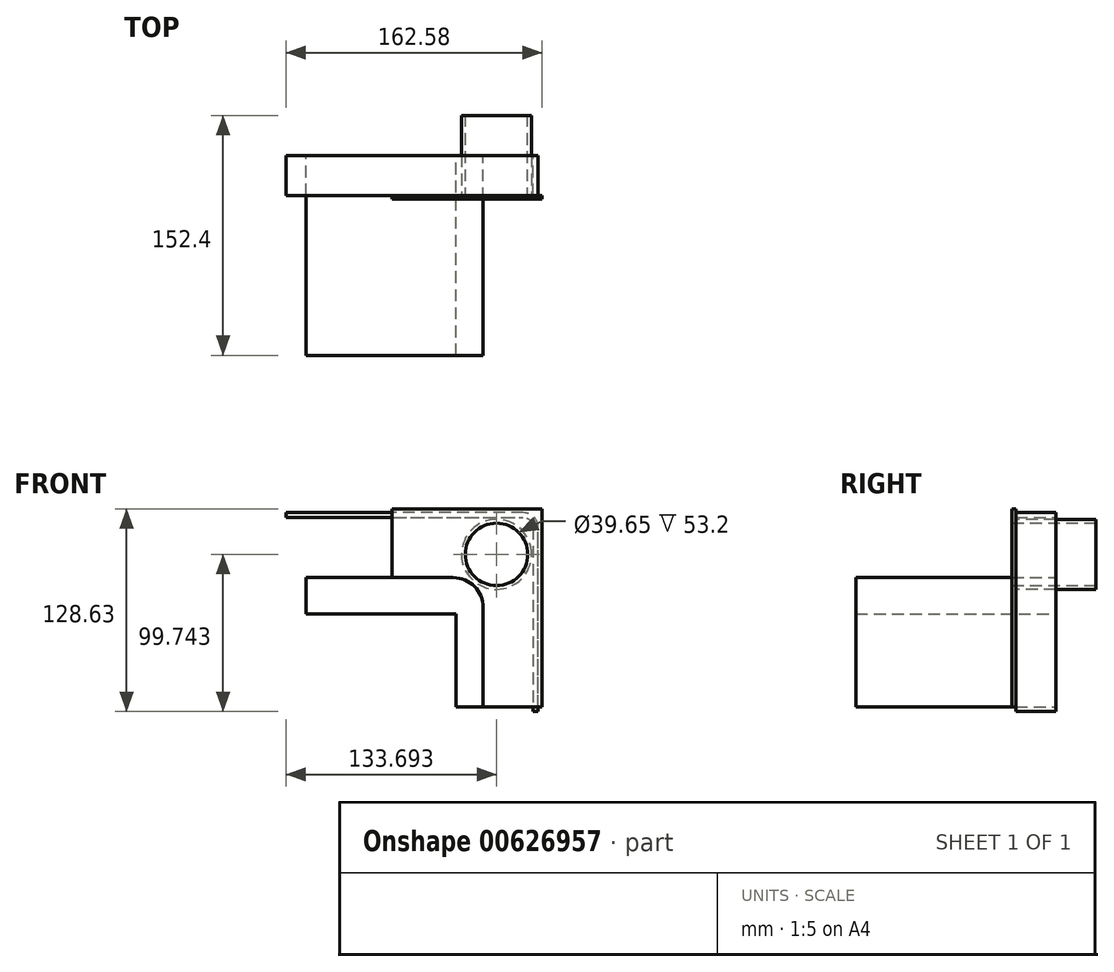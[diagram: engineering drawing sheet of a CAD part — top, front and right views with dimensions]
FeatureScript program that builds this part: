
annotation { "Feature Type Name" : "Feature", "Feature Type Description" : "" }
export const myFeature = defineFeature(function(context is Context, id is Id, definition is map)
    precondition{}
    {
        {
            var Q0;
            Q0=qCreatedBy(makeId("Front.planeOp"),FACE);
            var sketch = newSketch(context, id + "F0", { "sketchPlane" : qUnion([Q0])});
            skLineSegment(sketch, "E0", {"start": v(-125.26, 38.1) * mm, "end": v(25.4, 38.1) * mm});
            skLineSegment(sketch, "E1", {"start": v(31.75, 31.75) * mm, "end": v(31.75, -84.96) * mm});
            skLineSegment(sketch, "E2", {"start": v(31.75, -84.96) * mm, "end": v(34.92, -84.96) * mm});
            skLineSegment(sketch, "E3", {"start": v(34.92, -84.96) * mm, "end": v(34.92, 31.75) * mm});
            skLineSegment(sketch, "E4", {"start": v(25.4, 41.28) * mm, "end": v(-125.26, 41.27) * mm});
            skLineSegment(sketch, "E5", {"start": v(-125.26, 41.27) * mm, "end": v(-125.26, 38.1) * mm});
            skLineSegment(sketch, "E6", {"start": v(0, -19.05) * mm, "end": v(0, -82.22) * mm});
            skLineSegment(sketch, "E7", {"start": v(-19.05, 0) * mm, "end": v(-112.52, 0) * mm});
            skLineSegment(sketch, "E8", {"start": v(-112.52, 0) * mm, "end": v(-112.52, -22.95) * mm});
            skLineSegment(sketch, "E9", {"start": v(-112.52, -22.95) * mm, "end": v(-17.27, -22.95) * mm});
            skLineSegment(sketch, "E10", {"start": v(-17.27, -22.95) * mm, "end": v(-17.27, -82.22) * mm});
            skLineSegment(sketch, "E11", {"start": v(-17.27, -82.22) * mm, "end": v(0, -82.22) * mm});
            skPoint(sketch, "E12.visualSharp", {"position": v(31.75, 38.1) * mm});
            skArc(sketch, "E12.filletArc", {"start": v(31.75, 31.75) * mm, "mid": v(29.9, 36.24) * mm, "end": v(25.4, 38.1) * mm});
            skArc(sketch, "E13", {"start": v(25.4, 41.28) * mm, "mid": v(32.14, 38.49) * mm, "end": v(34.93, 31.75) * mm});
            skPoint(sketch, "E14.visualSharp", {"position": v(0, 0) * mm});
            skArc(sketch, "E14.filletArc", {"start": v(0, -19.05) * mm, "mid": v(-5.58, -5.58) * mm, "end": v(-19.05, 0) * mm});
            skSolve(sketch);
        }
        {
            var Q0;
            Q0=makeQuery(id+"F0.imprint","IMPRINT",FACE,{"disambiguationData":[TD([[makeQuery(id+"F0.imprint","IMPRINT",EDGE,{"derivedFrom":sQuery(id+"F0.wireOp",EDGE,"E6")}),-1.0]])]});
            extrude(context, id + "F1", {"entities" : qUnion([Q0]), "depth" : 127 * mm, "offsetDistance" : 25 * mm});
        }
        {
            var Q0;
            Q0=makeQuery(id+"F0.imprint","IMPRINT",FACE,{"disambiguationData":[TD([[makeQuery(id+"F0.imprint","IMPRINT",EDGE,{"derivedFrom":sQuery(id+"F0.wireOp",EDGE,"E0")}),1.0]])]});
            extrude(context, id + "F2", {"entities" : qUnion([Q0]), "depth" : 25.4 * mm, "offsetDistance" : 25 * mm});
        }
        {
            var Q0;
            Q0=makeQuery(id+"F2.opExtrude","CAP_FACE",FACE,{"disambiguationData":[OSD([sQuery(id+"F0.wireOp",EDGE,"E0"),sQuery(id+"F0.wireOp",EDGE,"E1"),sQuery(id+"F0.wireOp",EDGE,"E2"),sQuery(id+"F0.wireOp",EDGE,"E3"),sQuery(id+"F0.wireOp",EDGE,"E4"),sQuery(id+"F0.wireOp",EDGE,"E5"),sQuery(id+"F0.wireOp",EDGE,"E12.filletArc"),sQuery(id+"F0.wireOp",EDGE,"E13")])],"isStart":false});
            var sketch = newSketch(context, id + "F3", { "sketchPlane" : qUnion([Q0])});
            skCircle(sketch, "E15", {"center": v(8.43, 14.78) * mm, "radius": 22.23 * mm});
            skLineSegment(sketch, "E16", {"start": v(0, 0) * mm, "end": v(34.92, 41.28) * mm, "construction": true});
            skLineSegment(sketch, "E17", {"start": v(-57.8, 43.67) * mm, "end": v(-57.8, 0) * mm});
            skLineSegment(sketch, "E18", {"start": v(-57.8, 0) * mm, "end": v(-8.16, 0) * mm});
            skLineSegment(sketch, "E19", {"start": v(0, -82.01) * mm, "end": v(0, -5.78) * mm});
            skLineSegment(sketch, "E20", {"start": v(-57.8, 43.67) * mm, "end": v(37.32, 43.68) * mm});
            skLineSegment(sketch, "E21", {"start": v(37.32, 43.68) * mm, "end": v(37.33, -82.01) * mm});
            skLineSegment(sketch, "E22", {"start": v(37.32, -82.01) * mm, "end": v(0, -82.01) * mm});
            skCircle(sketch, "E23", {"center": v(8.43, 14.78) * mm, "radius": 19.83 * mm});
            skArc(sketch, "E24.0", {"start": v(0, -19.05) * mm, "mid": v(-5.58, -5.58) * mm, "end": v(-19.05, 0) * mm});
            skLineSegment(sketch, "E25", {"start": v(-7.04, -4.26) * mm, "end": v(-5.58, -2.47) * mm, "construction": true});
            skLineSegment(sketch, "E26", {"start": v(30.66, 14.78) * mm, "end": v(31.75, 14.78) * mm, "construction": true});
            skPoint(sketch, "E27", {"position": v(-5.58, -5.58) * mm});
            skLineSegment(sketch, "E28", {"start": v(8.43, 37) * mm, "end": v(8.43, 38.1) * mm, "construction": true});
            skSolve(sketch);
        }
        {
            var Q0;
            {var subQ11=makeQuery(id+"F2.opExtrude","CAP_EDGE",EDGE,{"disambiguationData":[OSD([sQuery(id+"F0.wireOp",EDGE,"E12.filletArc")])],"isStart":false});Q0=makeQuery(id+"F3.imprint","IMPRINT",FACE,{"disambiguationData":[TD([[makeQuery(id+"F3.imprint","IMPRINT",EDGE,{"derivedFrom":subQ11}),1.0]])]});}
            var Q1;
            {var subQ5=sQuery(id+"F3.wireOp",EDGE,"E24.0");Q1=makeQuery(id+"F3.imprint","IMPRINT",FACE,{"disambiguationData":[TD([[makeQuery(id+"F3.imprint","IMPRINT",EDGE,{"derivedFrom":subQ5}),-1.0]])]});}
            var Q2;
            {var subQ6=makeQuery(id+"F2.opExtrude","CAP_EDGE",EDGE,{"disambiguationData":[OSD([sQuery(id+"F0.wireOp",EDGE,"E12.filletArc")])],"isStart":false});Q2=makeQuery(id+"F3.imprint","IMPRINT",FACE,{"disambiguationData":[TD([[makeQuery(id+"F3.imprint","IMPRINT",EDGE,{"derivedFrom":subQ6}),-1.0]])]});}
            var Q3;
            {var subQ4=sQuery(id+"F3.wireOp",EDGE,"E20");Q3=makeQuery(id+"F3.imprint","IMPRINT",FACE,{"disambiguationData":[TD([[makeQuery(id+"F3.imprint","IMPRINT",EDGE,{"derivedFrom":subQ4}),-1.0]])]});}
            extrude(context, id + "F4", {"entities" : qUnion([Q0, Q1, Q2, Q3]), "depth" : 2.4 * mm, "offsetDistance" : 25 * mm});
        }
        {
            var Q0;
            Q0=makeQuery(id+"F3.imprint","IMPRINT",FACE,{"disambiguationData":[TD([[makeQuery(id+"F3.imprint","IMPRINT",EDGE,{"derivedFrom":sQuery(id+"F3.wireOp",EDGE,"E23")}),-1.0]])]});
            var Q1;
            Q1=makeQuery(id+"F4.opExtrude","CAP_FACE",FACE,{"disambiguationData":[OSD([sQuery(id+"F3.wireOp",EDGE,"E15"),sQuery(id+"F3.wireOp",EDGE,"E17"),sQuery(id+"F3.wireOp",EDGE,"E18"),sQuery(id+"F3.wireOp",EDGE,"E19"),sQuery(id+"F3.wireOp",EDGE,"E20"),sQuery(id+"F3.wireOp",EDGE,"E21"),sQuery(id+"F3.wireOp",EDGE,"E22"),sQuery(id+"F3.wireOp",EDGE,"E24.0")])],"isStart":false});
            extrude(context, id + "F5", {"entities" : qUnion([Q0]), "operationType" : NewBodyOperationType.ADD, "endBound" : BoundingType.UP_TO_SURFACE, "depth" : 10 * mm, "endBoundEntityFace" : qUnion([Q1]), "offsetDistance" : 25 * mm});
        }
        {
            var Q0;
            Q0=makeQuery(id+"F3.imprint","IMPRINT",FACE,{"disambiguationData":[TD([[makeQuery(id+"F3.imprint","IMPRINT",EDGE,{"derivedFrom":sQuery(id+"F3.wireOp",EDGE,"E23")}),-1.0]])]});
            extrude(context, id + "F6", {"entities" : qUnion([Q0]), "operationType" : NewBodyOperationType.ADD, "oppositeDirection" : true, "depth" : 50.8 * mm, "offsetDistance" : 25 * mm});
        }
        {
            var Q0;
            {var subQ4=sQuery(id+"F3.wireOp",EDGE,"E20");Q0=makeQuery(id+"F3.imprint","IMPRINT",FACE,{"disambiguationData":[TD([[makeQuery(id+"F3.imprint","IMPRINT",EDGE,{"derivedFrom":subQ4}),-1.0]])]});}
            extrude(context, id + "F7", {"entities" : qUnion([Q0]), "operationType" : NewBodyOperationType.ADD, "oppositeDirection" : true, "depth" : 1 / 50.8 * mm, "offsetDistance" : 25 * mm});
        }
    });
